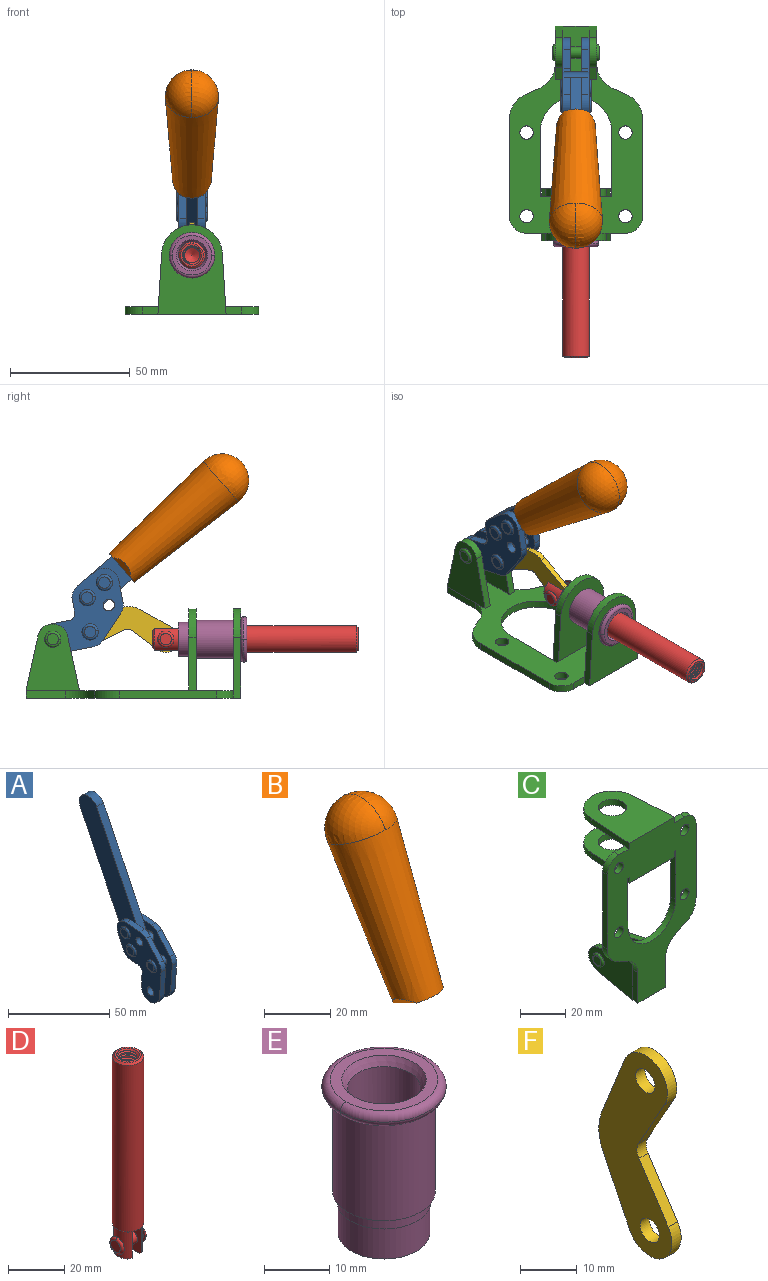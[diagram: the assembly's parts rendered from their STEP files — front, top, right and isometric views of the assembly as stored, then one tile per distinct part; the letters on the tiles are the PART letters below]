
ASSEMBLY  parts=6 mates=6
PART A: 59 faces, bbox 12.9x60.2x99.6 mm
  f0: torus R=2.39mm, axis (-1,0,0), area 14.9mm2, adj f20,f43,f51
  f1: torus R=2.39mm, axis (-1,0,0), area 14.9mm2, adj f19,f42,f51
  f2: torus R=2.39mm, axis (-1,0,0), area 14.9mm2, adj f18,f35,f51
  f3: torus R=2.39mm, axis (-1,0,0), area 14.9mm2, adj f14,f17,f23
  f4: torus R=2.39mm, axis (-1,0,0), area 14.9mm2, adj f13,f16,f23
  f5: torus R=2.39mm, axis (-1,0,0), area 14.9mm2, adj f12,f15,f23
  f6: cylinder r=2.39mm len=4.78mm, axis (1,0,0), area 46.5mm2, adj f48,f50,f51
  f7: cylinder r=2.39mm len=4.78mm, axis (1,0,0), area 46.5mm2, adj f50,f51
  f8: cylinder r=6.35mm len=12.68mm, axis (1,0,0), area 61.8mm2, adj f38,f39,f50,f51
  f9: cylinder r=2.39mm len=4.78mm, axis (-1,0,0), area 70.5mm2, adj f46,f50
  f10: cylinder r=2.39mm len=4.78mm, axis (-1,0,0), area 46.5mm2, adj f23,f45,f46
  f11: cylinder r=2.39mm len=4.78mm, axis (-1,0,0), area 46.5mm2, adj f23,f46
  f12: plane 4.78x4.78mm, normal (1,0,0), area 17.9mm2, adj f5,f15
  f13: plane 4.78x4.78mm, normal (1,0,0), area 17.9mm2, adj f4,f16
  f14: plane 4.78x4.78mm, normal (1,0,0), area 17.9mm2, adj f3,f17
  f15: torus R=2.39mm, axis (-1,0,0), area 14.9mm2, adj f5,f12,f23
  f16: torus R=2.39mm, axis (-1,0,0), area 14.9mm2, adj f4,f13,f23
  f17: torus R=2.39mm, axis (-1,0,0), area 14.9mm2, adj f3,f14,f23
  f18: plane 4.78x4.78mm, normal (-1,0,0), area 17.9mm2, adj f2,f35
  f19: plane 4.78x4.78mm, normal (-1,0,0), area 17.9mm2, adj f1,f42
  f20: plane 4.78x4.78mm, normal (-1,0,0), area 17.9mm2, adj f0,f43
  f21: plane 2.26x0.2mm, normal (1,0,0), area 0.2mm2, adj f31,f44
  f22: plane 2.26x0.2mm, normal (-1,0,0), area 0.2mm2, adj f41,f44
  f23: plane 39.37x30.77mm, normal (1,0,0), area 565.5mm2, adj f3,f4,f5,f10,f11,f15,f16,f17
  f24: cylinder r=6.1mm len=4.15mm, axis (-1,0,0), area 14.7mm2, adj f23,f25,f32,f46
  f25: plane 10.25x9.01mm, normal (0,-0.75,0.66), area 42.3mm2, adj f23,f24,f26,f46
  f26: cylinder r=6.35mm len=4.64mm, axis (-1,0,0), area 15.6mm2, adj f23,f25,f27,f46
  f27: plane 15.84x3.1mm, normal (0,-1,-0.07), area 49.2mm2, adj f23,f26,f28,f46
  f28: cylinder r=6.35mm len=12.68mm, axis (-1,0,0), area 61.8mm2, adj f23,f27,f29,f46
  f29: plane 8.11x3.1mm, normal (0,1,0.07), area 25.2mm2, adj f23,f28,f30,f46
  f30: cylinder r=3.05mm len=3.25mm, axis (-1,0,0), area 14.8mm2, adj f23,f29,f31,f46
  f31: plane 5.99x3.1mm, normal (0,0.07,-1), area 18.6mm2, adj f21,f23,f30,f44,f46
  f32: plane 9.5x3.1mm, normal (0,-0.07,1), area 29.5mm2, adj f23,f24,f33,f46,f47
  f33: cylinder r=6.1mm len=8.63mm, axis (-1,0,0), area 39.1mm2, adj f23,f32,f34,f47
  f34: plane 8.65x3.96mm, normal (0,0.91,-0.42), area 29.5mm2, adj f23,f33,f44,f47
  f35: torus R=2.39mm, axis (-1,0,0), area 14.9mm2, adj f2,f18,f51
  f36: plane 10.25x9.01mm, normal (0,-0.75,0.66), area 42.3mm2, adj f37,f49,f50,f51
  f37: cylinder r=6.35mm len=4.64mm, axis (1,0,0), area 15.6mm2, adj f36,f38,f50,f51
  f38: plane 15.84x3.1mm, normal (0,-1,-0.07), area 49.2mm2, adj f8,f37,f50,f51
  f39: plane 8.11x3.1mm, normal (0,1,0.07), area 25.2mm2, adj f8,f40,f50,f51
  f40: cylinder r=3.05mm len=3.25mm, axis (1,0,0), area 14.8mm2, adj f39,f41,f50,f51
  f41: plane 5.99x3.1mm, normal (0,0.07,-1), area 18.6mm2, adj f22,f40,f44,f50,f51
  f42: torus R=2.39mm, axis (-1,0,0), area 14.9mm2, adj f1,f19,f51
  f43: torus R=2.39mm, axis (-1,0,0), area 14.9mm2, adj f0,f20,f51
  f44: cylinder r=6.35mm len=12.12mm, axis (-1,0,0), area 128.9mm2, adj f21,f22,f23,f31,f34,f41,f46,f47
  f45: plane 2.65x1.35mm, normal (1,0,0), area 1mm2, adj f10,f55
  f46: plane 39.08x20.42mm, normal (-1,0,0), area 412.5mm2, adj f9,f10,f11,f24,f25,f26,f27,f28
  f47: plane 77.62x39.82mm, normal (1,0,0), area 850mm2, adj f32,f33,f34,f44,f53,f54,f55
  f48: plane 2.65x1.35mm, normal (-1,0,0), area 1mm2, adj f6,f55
  f49: cylinder r=6.1mm len=4.15mm, axis (1,0,0), area 14.7mm2, adj f36,f50,f51,f56
  f50: plane 39.08x20.42mm, normal (1,0,0), area 412.5mm2, adj f6,f7,f8,f9,f36,f37,f38,f39
  f51: plane 39.37x30.77mm, normal (-1,0,0), area 565.5mm2, adj f0,f1,f2,f6,f7,f8,f35,f36
  f52: plane 8.65x3.96mm, normal (0,0.91,-0.42), area 29.5mm2, adj f44,f51,f57,f58
  f53: plane 68.49x33.4mm, normal (0,0.9,-0.44), area 358.1mm2, adj f44,f47,f54,f58
  f54: cylinder r=6.35mm len=12.06mm, axis (1,0,0), area 93.7mm2, adj f47,f53,f55,f58
  f55: plane 68.49x33.4mm, normal (0,-0.9,0.44), area 358.1mm2, adj f44,f45,f46,f47,f48,f50,f54,f58
  f56: plane 9.5x3.1mm, normal (0,-0.07,1), area 29.5mm2, adj f49,f50,f51,f57,f58
  f57: cylinder r=6.1mm len=8.63mm, axis (1,0,0), area 39.1mm2, adj f51,f52,f56,f58
  f58: plane 77.62x39.82mm, normal (-1,0,0), area 850mm2, adj f44,f52,f53,f54,f55,f56,f57
PART B: 11 faces, bbox 22.3x42.6x64.5 mm
  f0: sphere r=11.13mm, area 411.4mm2, adj f1,f8
  f1: cone r=11.11mm half-angle=3.3deg, axis (0,0.44,0.9), area 3251.8mm2, adj f0,f7,f8,f9,f10
  f2: cylinder r=6.16mm len=11.7mm, axis (1,0,0), area 89.5mm2, adj f3,f4,f5,f6
  f3: plane 60.23x36.75mm, normal (-1,0,0), area 763.6mm2, adj f2,f4,f6,f10
  f4: plane 51.37x25.05mm, normal (0,0.9,-0.44), area 264.2mm2, adj f2,f3,f5,f10
  f5: plane 60.23x36.75mm, normal (1,0,0), area 763.6mm2, adj f2,f4,f6,f10
  f6: plane 51.37x25.05mm, normal (0,-0.9,0.44), area 264.2mm2, adj f2,f3,f5,f10
  f7: plane 9.95x5.95mm, normal (0.71,-0.31,-0.64), area 25.8mm2, adj f1,f10
  f8: sphere r=11.13mm, area 411.4mm2, adj f0,f1
  f9: plane 9.95x5.95mm, normal (-0.71,-0.31,-0.64), area 25.8mm2, adj f1,f10
  f10: plane 14.27x11.38mm, normal (0,-0.44,-0.9), area 106.7mm2, adj f1,f3,f4,f5,f6,f7,f9
PART C: 55 faces, bbox 55.7x37.4x89.8 mm
  f0: torus R=2.41mm, axis (-1,0,0), area 15mm2, adj f11,f15,f25
  f1: torus R=2.41mm, axis (-1,0,0), area 15mm2, adj f10,f12,f22
  f2: cylinder r=2.78mm len=5.56mm, axis (0,-1,0), area 54.2mm2, adj f30,f54
  f3: cylinder r=14.99mm len=29.97mm, axis (0,-1,0), area 145.9mm2, adj f30,f49,f53,f54
  f4: cylinder r=2.78mm len=5.56mm, axis (0,-1,0), area 54.2mm2, adj f30,f54
  f5: cylinder r=2.78mm len=5.56mm, axis (0,-1,0), area 54.2mm2, adj f30,f54
  f6: cylinder r=2.78mm len=5.56mm, axis (0,-1,0), area 54.2mm2, adj f30,f54
  f7: cylinder r=6.35mm len=12.7mm, axis (0,0,1), area 123.6mm2, adj f27,f51
  f8: cylinder r=6.35mm len=12.7mm, axis (0,0,-1), area 124.7mm2, adj f21,f35
  f9: cylinder r=2.41mm len=11.18mm, axis (-1,0,0), area 169.4mm2, adj f16,f19
  f10: plane 4.83x4.83mm, normal (1,0,0), area 18.3mm2, adj f1,f12
  f11: plane 4.83x4.83mm, normal (-1,0,0), area 18.3mm2, adj f0,f15
  f12: torus R=2.41mm, axis (-1,0,0), area 15mm2, adj f1,f10,f22
  f13: cylinder r=6.35mm len=12.41mm, axis (1,0,0), area 53.4mm2, adj f18,f19,f22,f23
  f14: cylinder r=6.35mm len=12.41mm, axis (-1,0,0), area 53.4mm2, adj f16,f17,f24,f25
  f15: torus R=2.41mm, axis (-1,0,0), area 15mm2, adj f0,f11,f25
  f16: plane 27.86x22.35mm, normal (1,0,0), area 425.4mm2, adj f9,f14,f17,f24,f30
  f17: plane 22.86x4.97mm, normal (0,0.21,0.98), area 72.5mm2, adj f14,f16,f25,f30
  f18: plane 22.86x4.97mm, normal (0,0.21,0.98), area 72.5mm2, adj f13,f19,f22,f30
  f19: plane 27.86x22.35mm, normal (-1,0,0), area 425.4mm2, adj f9,f13,f18,f23,f30
  f20: cylinder r=12.7mm len=25.35mm, axis (0,0,-1), area 119.8mm2, adj f21,f34,f35,f36
  f21: plane 34.21x28.07mm, normal (0,0,-1), area 702.4mm2, adj f8,f20,f30,f34,f36
  f22: plane 27.96x22.45mm, normal (1,0,0), area 407.2mm2, adj f1,f12,f13,f18,f23,f30,f42,f43
  f23: plane 22.86x4.97mm, normal (0,0.21,-0.98), area 72.5mm2, adj f13,f19,f22,f44
  f24: plane 22.86x4.97mm, normal (0,0.21,-0.98), area 72.5mm2, adj f14,f16,f25,f44
  f25: plane 27.86x22.35mm, normal (-1,0,0), area 407.1mm2, adj f0,f14,f15,f17,f24,f30,f45,f46
  f26: plane 3.1x0.95mm, normal (0,0,-1), area 2.7mm2, adj f30,f49,f50,f54
  f27: plane 34.21x28.07mm, normal (0,0,1), area 702.4mm2, adj f7,f28,f30,f50,f52
  f28: cylinder r=12.7mm len=25.35mm, axis (0,0,1), area 118.8mm2, adj f27,f50,f51,f52
  f29: plane 3.1x0.95mm, normal (0,0,-1), area 2.7mm2, adj f30,f52,f53,f54
  f30: plane 86.54x55.63mm, normal (0,1,0), area 2362.9mm2, adj f2,f3,f4,f5,f6,f16,f17,f18
  f31: plane 40.56x3.1mm, normal (-1,0,0), area 125.7mm2, adj f30,f32,f48,f54
  f32: cylinder r=7.11mm len=7.11mm, axis (0,-1,0), area 34.6mm2, adj f30,f31,f33,f54
  f33: plane 6.67x3.1mm, normal (0,0,1), area 20.4mm2, adj f30,f32,f34,f54
  f34: plane 25.39x3.13mm, normal (-1,0.06,0), area 79.5mm2, adj f20,f21,f33,f35,f54
  f35: plane 37.31x28.45mm, normal (0,0,1), area 789.9mm2, adj f8,f20,f34,f36,f54
  f36: plane 25.39x3.13mm, normal (1,0.06,0), area 79.5mm2, adj f20,f21,f35,f37,f54
  f37: plane 6.67x3.1mm, normal (0,0,1), area 20.4mm2, adj f30,f36,f38,f54
  f38: cylinder r=7.11mm len=7.11mm, axis (0,-1,0), area 34.6mm2, adj f30,f37,f39,f54
  f39: plane 40.56x3.1mm, normal (1,0,0), area 125.7mm2, adj f30,f38,f40,f54
  f40: cylinder r=11.18mm len=10.16mm, axis (0,-1,0), area 39.5mm2, adj f30,f39,f41,f54
  f41: plane 6.09x3.1mm, normal (0.42,0,-0.91), area 20.8mm2, adj f30,f40,f42,f54
  f42: cylinder r=11.18mm len=9.41mm, axis (0,-1,0), area 37.2mm2, adj f22,f30,f41,f43,f54
  f43: plane 16.5x3.1mm, normal (1,0,0), area 51.1mm2, adj f22,f42,f44,f54
  f44: plane 17.37x3.1mm, normal (0,0,-1), area 53.8mm2, adj f23,f24,f30,f43,f45,f54
  f45: plane 16.5x3.1mm, normal (-1,0,0), area 51.1mm2, adj f25,f44,f46,f54
  f46: cylinder r=11.18mm len=9.41mm, axis (0,-1,0), area 37.2mm2, adj f25,f30,f45,f47,f54
  f47: plane 6.09x3.1mm, normal (-0.42,0,-0.91), area 20.8mm2, adj f30,f46,f48,f54
  f48: cylinder r=11.18mm len=10.16mm, axis (0,-1,0), area 39.5mm2, adj f30,f31,f47,f54
  f49: plane 26.54x3.1mm, normal (-1,0,0), area 82.3mm2, adj f3,f26,f30,f54
  f50: plane 25.39x3.1mm, normal (1,0.06,0), area 78.8mm2, adj f26,f27,f28,f51,f54
  f51: plane 37.31x28.45mm, normal (0,0,-1), area 789.9mm2, adj f7,f28,f50,f52,f54
  f52: plane 25.39x3.1mm, normal (-1,0.06,0), area 78.8mm2, adj f27,f28,f29,f51,f54
  f53: plane 26.54x3.1mm, normal (1,0,0), area 82.3mm2, adj f3,f29,f30,f54
  f54: plane 89.66x55.63mm, normal (0,-1,0), area 2678.5mm2, adj f2,f3,f4,f5,f6,f26,f29,f31
PART D: 48 faces, bbox 12.6x11.1x86.1 mm
  f0: torus R=2.41mm, axis (-1,0,0), area 15mm2, adj f30,f32,f34
  f1: torus R=2.41mm, axis (-1,0,0), area 15mm2, adj f29,f31,f33
  f2: cylinder r=5.54mm len=72.39mm, axis (0,0,1), area 2518.5mm2, adj f3,f4,f42,f43
  f3: cone r=5.54mm half-angle=45deg, axis (0,0,1), area 7.6mm2, adj f2,f5,f41
  f4: cone r=5.54mm half-angle=45deg, axis (0,0,-1), area 34.9mm2, adj f2,f39
  f5: cylinder r=5.08mm len=11.48mm, axis (0,0,1), area 108.3mm2, adj f3,f7,f8,f41
  f6: cylinder r=2.41mm len=4.83mm, axis (-1,0,0), area 71.2mm2, adj f40,f41
  f7: cylinder r=2.41mm len=4.83mm, axis (-1,0,0), area 7.6mm2, adj f5,f34
  f8: cone r=5.08mm half-angle=45deg, axis (0,0,1), area 10.6mm2, adj f5,f37,f41
  f9: cone r=3.98mm half-angle=45deg, axis (0,0,1), area 17.6mm2, adj f27,f39,f45,f46,f47
  f10: cylinder r=2.41mm len=4.83mm, axis (-1,0,0), area 7.6mm2, adj f33,f38
  f11: cylinder r=3.2mm len=6.4mm, axis (0,0,1), area 78.4mm2, adj f12,f28,f44,f45,f47
  f12: cylinder r=3.2mm len=6.4mm, axis (0,0,1), area 10.5mm2, adj f11,f13,f45,f47
  f13: cylinder r=3.2mm len=6.4mm, axis (0,0,1), area 10.5mm2, adj f12,f14,f45,f47
  f14: cylinder r=3.2mm len=6.4mm, axis (0,0,1), area 10.5mm2, adj f13,f15,f45,f47
  f15: cylinder r=3.2mm len=6.4mm, axis (0,0,1), area 10.5mm2, adj f14,f16,f45,f47
  f16: cylinder r=3.2mm len=6.4mm, axis (0,0,1), area 10.5mm2, adj f15,f17,f45,f47
  f17: cylinder r=3.2mm len=6.4mm, axis (0,0,1), area 10.5mm2, adj f16,f18,f45,f47
  f18: cylinder r=3.2mm len=6.4mm, axis (0,0,1), area 10.5mm2, adj f17,f19,f45,f47
  f19: cylinder r=3.2mm len=6.4mm, axis (0,0,1), area 10.5mm2, adj f18,f20,f45,f47
  f20: cylinder r=3.2mm len=6.4mm, axis (0,0,1), area 10.5mm2, adj f19,f21,f45,f47
  f21: cylinder r=3.2mm len=6.4mm, axis (0,0,1), area 10.5mm2, adj f20,f22,f45,f47
  f22: cylinder r=3.2mm len=6.4mm, axis (0,0,1), area 10.5mm2, adj f21,f23,f45,f47
  f23: cylinder r=3.2mm len=6.4mm, axis (0,0,1), area 10.5mm2, adj f22,f24,f45,f47
  f24: cylinder r=3.2mm len=6.4mm, axis (0,0,1), area 10.5mm2, adj f23,f25,f45,f47
  f25: cylinder r=3.2mm len=6.4mm, axis (0,0,1), area 10.5mm2, adj f24,f26,f45,f47
  f26: cylinder r=3.2mm len=6.4mm, axis (0,0,1), area 10.5mm2, adj f25,f27,f45,f47
  f27: cylinder r=3.2mm len=6.4mm, axis (0,0,1), area 7.4mm2, adj f9,f26,f45,f47
  f28: cone r=3.2mm half-angle=60deg, axis (0,0,1), area 37.2mm2, adj f11
  f29: plane 4.83x4.83mm, normal (-1,0,0), area 18.3mm2, adj f1,f31
  f30: plane 4.83x4.83mm, normal (1,0,0), area 18.3mm2, adj f0,f32
  f31: torus R=2.41mm, axis (-1,0,0), area 15mm2, adj f1,f29,f33
  f32: torus R=2.41mm, axis (-1,0,0), area 15mm2, adj f0,f30,f34
  f33: plane 6.83x6.83mm, normal (1,0,0), area 18.3mm2, adj f1,f10,f31
  f34: plane 6.83x6.83mm, normal (-1,0,0), area 18.3mm2, adj f0,f7,f32
  f35: cone r=5.08mm half-angle=45deg, axis (0,0,1), area 10.6mm2, adj f36,f38,f40
  f36: plane 7.25x1.97mm, normal (0,0,-1), area 10mm2, adj f35,f40
  f37: plane 7.25x1.97mm, normal (0,0,-1), area 10mm2, adj f8,f41
  f38: cylinder r=5.08mm len=11.48mm, axis (0,0,1), area 108.3mm2, adj f10,f35,f40,f42
  f39: plane 9.55x9.55mm, normal (0,0,1), area 22mm2, adj f4,f9
  f40: plane 12.76x10.09mm, normal (1,0,0), area 95.7mm2, adj f6,f35,f36,f38,f42,f43
  f41: plane 12.76x10.09mm, normal (-1,0,0), area 95.7mm2, adj f3,f5,f6,f8,f37,f43
  f42: cone r=5.54mm half-angle=45deg, axis (0,0,1), area 7.6mm2, adj f2,f38,f40
  f43: plane 11.07x4.7mm, normal (0,0,-1), area 50.4mm2, adj f2,f40,f41
  f44: plane 0.89x0.62mm, normal (-1,0,0), area 0.3mm2, adj f11,f45,f46,f47
  f45: bspline ~24.8x7.63mm, area 266.6mm2, adj f9,f11,f12,f13,f14,f15,f16,f17
  f46: bspline ~24.87x7.63mm, area 73.6mm2, adj f9,f44,f45,f47
  f47: bspline ~24.98x7.63mm, area 272.5mm2, adj f9,f11,f12,f13,f14,f15,f16,f17
PART E: 15 faces, bbox 20.6x20.6x28.7 mm
  f0: torus R=8.26mm, axis (0,0,1), area 56.8mm2, adj f1,f10,f12
  f1: torus R=8.26mm, axis (0,0,1), area 56.8mm2, adj f0,f6,f13
  f2: cylinder r=5.59mm len=25.91mm, axis (0,0,1), area 909.6mm2, adj f3,f4
  f3: cone r=6.86mm half-angle=45deg, axis (0,0,-1), area 70.2mm2, adj f2,f14
  f4: cone r=6.47mm half-angle=30deg, axis (0,0,1), area 66.7mm2, adj f2,f13
  f5: cylinder r=7.04mm len=14.07mm, axis (0,0,1), area 252.6mm2, adj f11,f14
  f6: torus R=8.26mm, axis (0,0,1), area 56.8mm2, adj f1,f12,f13
  f7: cylinder r=7.16mm len=14.33mm, axis (0,0,1), area 91.5mm2, adj f9,f11
  f8: cylinder r=7.86mm len=18.42mm, axis (0,0,1), area 909.6mm2, adj f9,f10
  f9: plane 15.72x15.72mm, normal (0,0,-1), area 33mm2, adj f7,f8
  f10: plane 16.51x16.51mm, normal (0,0,-1), area 19.9mm2, adj f0,f8,f12
  f11: plane 14.33x14.33mm, normal (0,0,-1), area 5.7mm2, adj f5,f7
  f12: torus R=8.26mm, axis (0,0,1), area 56.8mm2, adj f0,f6,f10
  f13: plane 16.51x16.51mm, normal (0,0,1), area 82.7mm2, adj f1,f4,f6
  f14: plane 14.07x14.07mm, normal (0,0,-1), area 7.8mm2, adj f3,f5
PART F: 12 faces, bbox 2.3x18.2x42.8 mm
  f0: cylinder r=2.4mm len=4.8mm, axis (1,0,0), area 34.9mm2, adj f4,f11
  f1: cylinder r=10.41mm len=8.47mm, axis (1,0,0), area 20.2mm2, adj f4,f9,f10,f11
  f2: cylinder r=3.05mm len=3.16mm, axis (1,0,0), area 7.7mm2, adj f4,f6,f7,f11
  f3: cylinder r=2.4mm len=4.8mm, axis (1,0,0), area 34.9mm2, adj f4,f11
  f4: plane 42.81x18.23mm, normal (-1,0,0), area 414.1mm2, adj f0,f1,f2,f3,f5,f6,f7,f8
  f5: cylinder r=5.54mm len=10.67mm, axis (1,0,0), area 41.8mm2, adj f4,f6,f10,f11
  f6: plane 11.66x6.53mm, normal (0,-0.87,-0.49), area 30.9mm2, adj f2,f4,f5,f11
  f7: plane 11.17x7.33mm, normal (0,-0.84,0.55), area 30.9mm2, adj f2,f4,f8,f11
  f8: cylinder r=5.54mm len=10.51mm, axis (1,0,0), area 41.8mm2, adj f4,f7,f9,f11
  f9: plane 13.67x6.67mm, normal (0,0.9,-0.44), area 35.1mm2, adj f1,f4,f8,f11
  f10: plane 14.1x5.7mm, normal (0,0.93,0.37), area 35.1mm2, adj f1,f4,f5,f11
  f11: plane 42.81x18.23mm, normal (1,0,0), area 414.1mm2, adj f0,f1,f2,f3,f5,f6,f7,f8
PLACE A rot(axis=(1,0,0),75deg) t=(0,3.86,9.14)mm
PLACE B rot(axis=(1,0,0),75deg) t=(-0.04,3.86,9.14)mm
PLACE C rot(axis=(1,0,0),90deg) t=(0,9.14,0)mm fixed
PLACE D rot(axis=(1,0,0),90deg) t=(0,9.52,0)mm
PLACE E rot(axis=(1,0,0),90deg) t=(0,9.14,0)mm
PLACE F rot(axis=(1,0,0),97.5deg) t=(0,12.59,2.22)mm
MATE revolute F.f3 <-> A.f4  axis (1,0,0) through (0,25.65,27.64)mm
MATE fastened B.f2 <-> A.f54  axis (1,0,0) through (-2.35,-30.66,91.94)mm
MATE slider D.f2 <-> C.f7  axis (0,-1,0) through (0,-49.26,24.61)mm
MATE fastened E.f2 <-> C.f7  axis (0,1,0) through (0,-37.25,24.61)mm
MATE revolute D.f6 <-> F.f5  axis (-1,0,0) through (0,-5.96,24.61)mm
MATE revolute C.f0 <-> A.f7  axis (-1,0,0) through (0,41.23,24.61)mm
